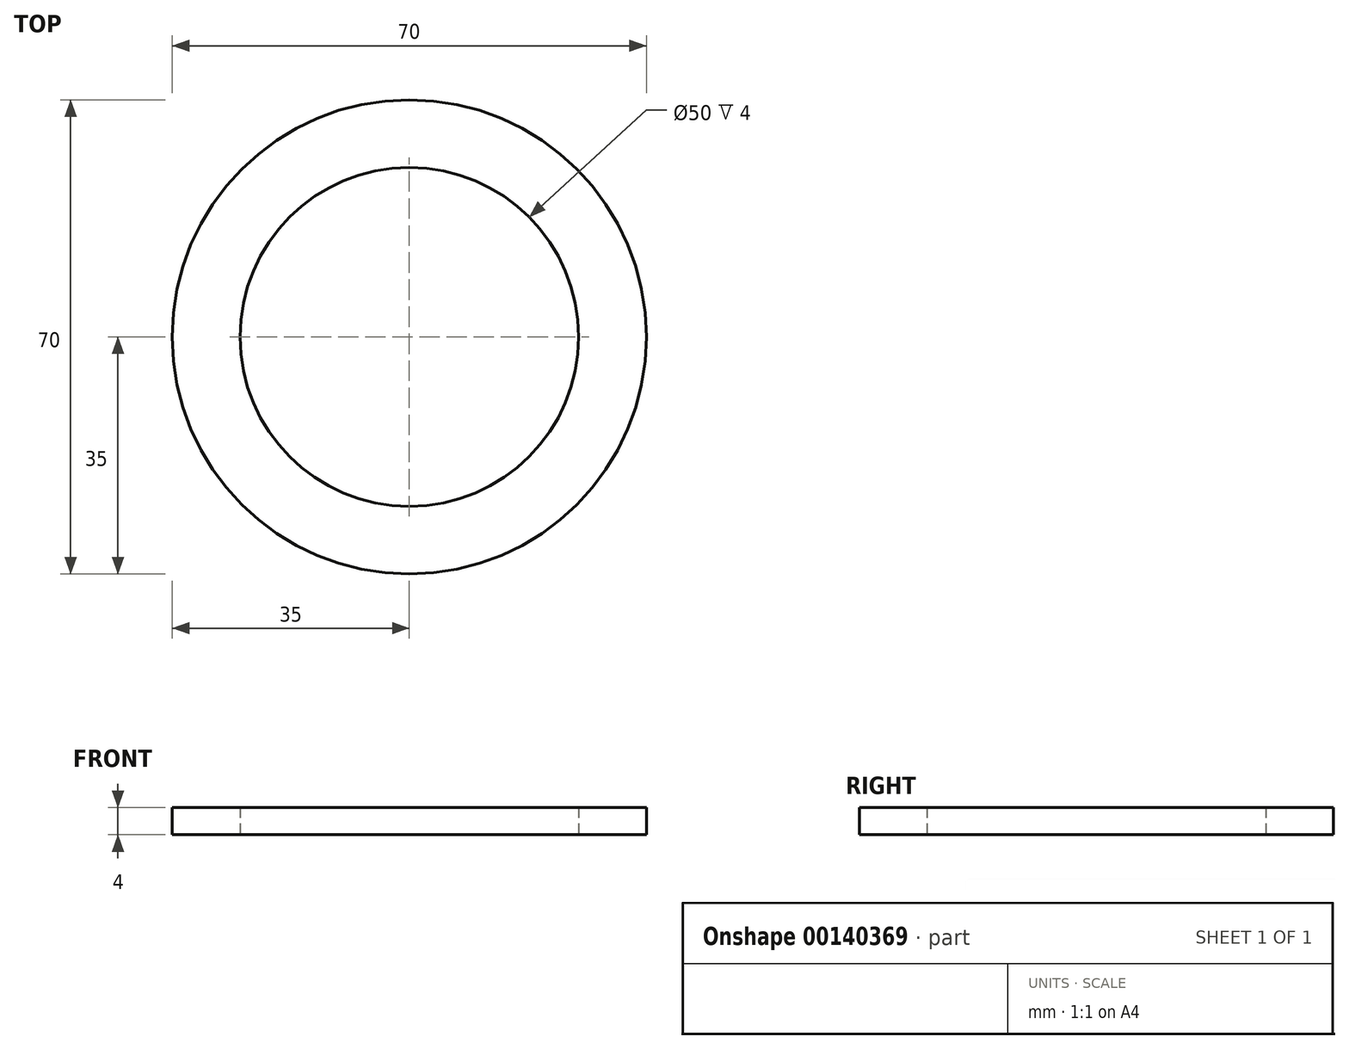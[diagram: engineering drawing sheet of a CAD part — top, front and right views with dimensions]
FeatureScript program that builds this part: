
annotation { "Feature Type Name" : "Feature", "Feature Type Description" : "" }
export const myFeature = defineFeature(function(context is Context, id is Id, definition is map)
    precondition{}
    {
        {
            var Q0;
            Q0=qCreatedBy(makeId("Top.planeOp"),FACE);
            var sketch = newSketch(context, id + "F0", { "sketchPlane" : qUnion([Q0])});
            skCircle(sketch, "E0", {"center": v(0, 0) * mm, "radius": 35 * mm});
            skCircle(sketch, "E1", {"center": v(0, 0) * mm, "radius": 25 * mm});
            skSolve(sketch);
        }
        {
            var Q0;
            Q0 = qSketchRegion(id + "F0", true);
            extrude(context, id + "F1", {"entities" : qUnion([Q0]), "depth" : 4 * mm});
        }
    });
